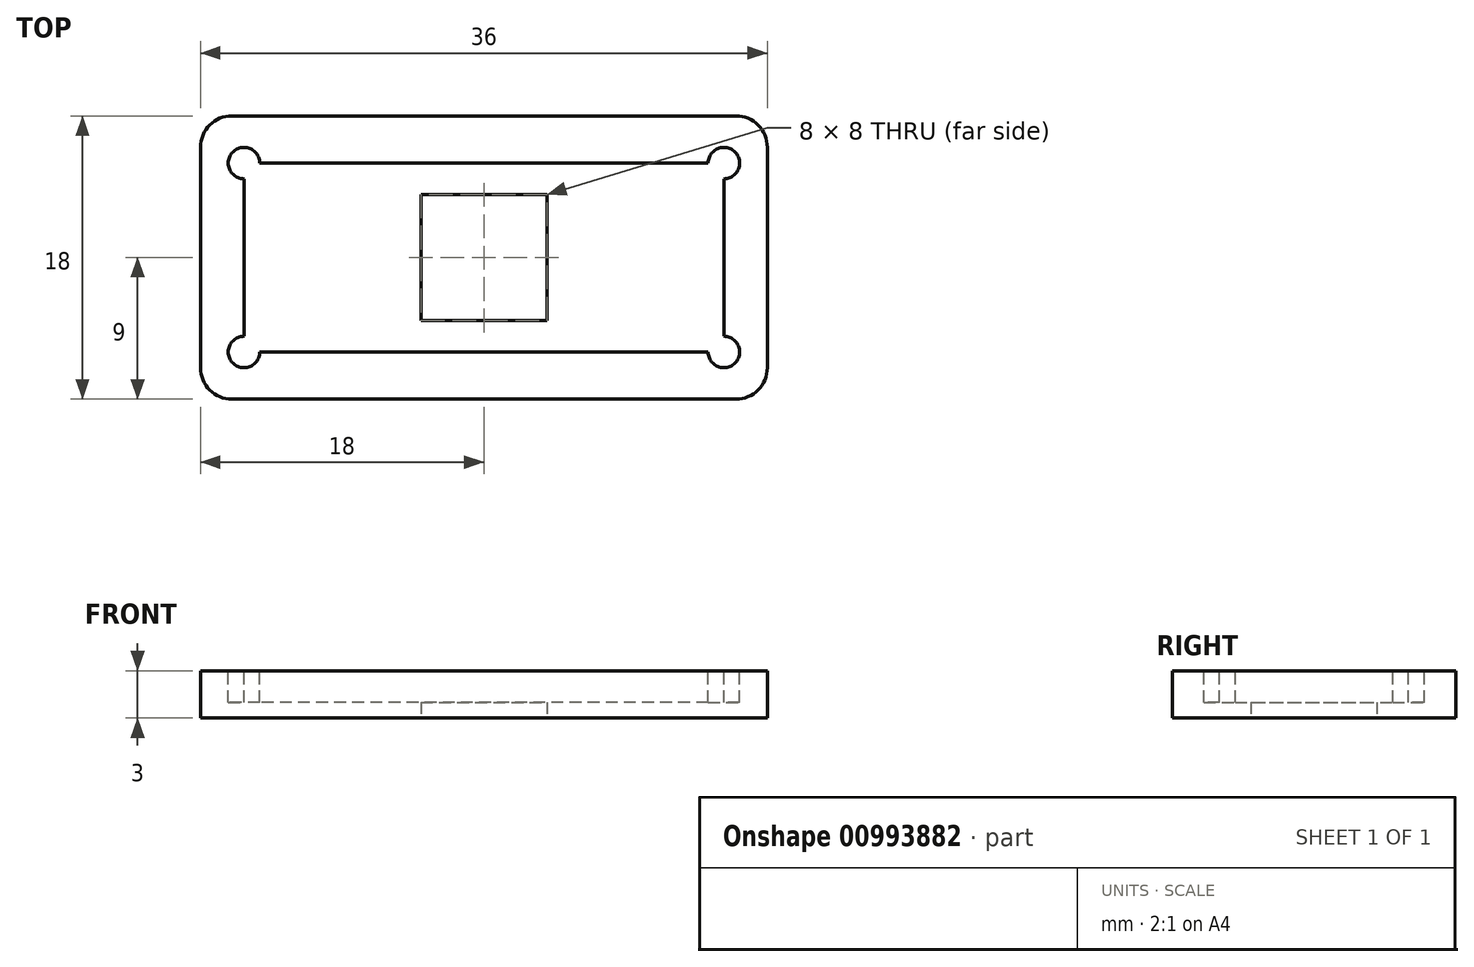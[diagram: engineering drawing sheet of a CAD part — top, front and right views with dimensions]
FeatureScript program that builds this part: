
annotation { "Feature Type Name" : "Feature", "Feature Type Description" : "" }
export const myFeature = defineFeature(function(context is Context, id is Id, definition is map)
    precondition{}
    {
        {
            var Q0;
            Q0=qCreatedBy(makeId("Top.planeOp"),FACE);
            var sketch = newSketch(context, id + "F0", { "sketchPlane" : qUnion([Q0])});
            skLineSegment(sketch, "E0.bottom", {"start": v(18, -9) * mm, "end": v(-18, -9) * mm});
            skLineSegment(sketch, "E0.top", {"start": v(18, 9) * mm, "end": v(-18, 9) * mm});
            skLineSegment(sketch, "E0.left", {"start": v(18, -9) * mm, "end": v(18, 9) * mm});
            skLineSegment(sketch, "E0.right", {"start": v(-18, -9) * mm, "end": v(-18, 9) * mm});
            skPoint(sketch, "E0.middle", {"position": v(0, 0) * mm});
            skSolve(sketch);
        }
        {
            var Q0;
            Q0=makeQuery(id+"F0.imprint","IMPRINT",FACE,{"disambiguationData":[TD([[makeQuery(id+"F0.imprint","IMPRINT",EDGE,{"derivedFrom":sQuery(id+"F0.wireOp",EDGE,"E0.bottom")}),-1.0]])]});
            extrude(context, id + "F1", {"entities" : qUnion([Q0]), "depth" : 3 * mm, "offsetDistance" : 25 * mm});
        }
        {
            var Q0;
            Q0=makeQuery(id+"F1.opExtrude","CAP_FACE",FACE,{"disambiguationData":[OSD([sQuery(id+"F0.wireOp",EDGE,"E0.bottom"),sQuery(id+"F0.wireOp",EDGE,"E0.top"),sQuery(id+"F0.wireOp",EDGE,"E0.left"),sQuery(id+"F0.wireOp",EDGE,"E0.right")])],"isStart":false});
            var sketch = newSketch(context, id + "F2", { "sketchPlane" : qUnion([Q0])});
            skLineSegment(sketch, "E1.bottom", {"start": v(15.24, -6) * mm, "end": v(-15.24, -6) * mm});
            skLineSegment(sketch, "E1.top", {"start": v(15.24, 6) * mm, "end": v(-15.24, 6) * mm});
            skLineSegment(sketch, "E1.left", {"start": v(15.24, -6) * mm, "end": v(15.24, 6) * mm});
            skLineSegment(sketch, "E1.right", {"start": v(-15.24, -6) * mm, "end": v(-15.24, 6) * mm});
            skPoint(sketch, "E1.middle", {"position": v(0, 0) * mm});
            skSolve(sketch);
        }
        {
            var Q0;
            Q0=makeQuery(id+"F2.imprint","IMPRINT",FACE,{"disambiguationData":[TD([[makeQuery(id+"F2.imprint","IMPRINT",EDGE,{"derivedFrom":sQuery(id+"F2.wireOp",EDGE,"E1.bottom")}),-1.0]])]});
            extrude(context, id + "F3", {"entities" : qUnion([Q0]), "operationType" : NewBodyOperationType.REMOVE, "oppositeDirection" : true, "depth" : 2 * mm, "offsetDistance" : 25 * mm});
        }
        {
            var Q0;
            Q0=makeQuery(id+"F1.opExtrude","CAP_FACE",FACE,{"disambiguationData":[OSD([sQuery(id+"F0.wireOp",EDGE,"E0.bottom"),sQuery(id+"F0.wireOp",EDGE,"E0.top"),sQuery(id+"F0.wireOp",EDGE,"E0.left"),sQuery(id+"F0.wireOp",EDGE,"E0.right")])],"isStart":true});
            var sketch = newSketch(context, id + "F4", { "sketchPlane" : qUnion([Q0])});
            skLineSegment(sketch, "E2.bottom", {"start": v(4, -4) * mm, "end": v(-4, -4) * mm});
            skLineSegment(sketch, "E2.top", {"start": v(4, 4) * mm, "end": v(-4, 4) * mm});
            skLineSegment(sketch, "E2.left", {"start": v(4, -4) * mm, "end": v(4, 4) * mm});
            skLineSegment(sketch, "E2.right", {"start": v(-4, -4) * mm, "end": v(-4, 4) * mm});
            skPoint(sketch, "E2.middle", {"position": v(0, 0) * mm});
            skSolve(sketch);
        }
        {
            var Q0;
            Q0 = qSketchRegion(id + "F4", true);
            extrude(context, id + "F5", {"entities" : qUnion([Q0]), "operationType" : NewBodyOperationType.REMOVE, "endBound" : BoundingType.THROUGH_ALL, "oppositeDirection" : true, "depth" : 25 * mm, "offsetDistance" : 25 * mm});
        }
        {
            var Q0;
            Q0=makeQuery(id+"F1.opExtrude","SWEPT_EDGE",EDGE,{"disambiguationData":[OSD([sQuery(id+"F0.wireOp",EDGE,"E0.bottom"),sQuery(id+"F0.wireOp",EDGE,"E0.right")])]});
            var Q1;
            Q1=makeQuery(id+"F1.opExtrude","SWEPT_EDGE",EDGE,{"disambiguationData":[OSD([sQuery(id+"F0.wireOp",EDGE,"E0.top"),sQuery(id+"F0.wireOp",EDGE,"E0.right")])]});
            var Q2;
            Q2=makeQuery(id+"F1.opExtrude","SWEPT_EDGE",EDGE,{"disambiguationData":[OSD([sQuery(id+"F0.wireOp",EDGE,"E0.bottom"),sQuery(id+"F0.wireOp",EDGE,"E0.left")])]});
            var Q3;
            Q3=makeQuery(id+"F1.opExtrude","SWEPT_EDGE",EDGE,{"disambiguationData":[OSD([sQuery(id+"F0.wireOp",EDGE,"E0.top"),sQuery(id+"F0.wireOp",EDGE,"E0.left")])]});
            fillet(context, id + "F6", {"entities" : qUnion([Q0, Q1, Q2, Q3]), "radius" : 2 * mm, "tangentPropagation" : true, "allowEdgeOverflow" : false});
        }
        {
            var Q0;
            Q0=makeQuery(id+"F1.opExtrude","CAP_FACE",FACE,{"disambiguationData":[OSD([sQuery(id+"F0.wireOp",EDGE,"E0.bottom"),sQuery(id+"F0.wireOp",EDGE,"E0.top"),sQuery(id+"F0.wireOp",EDGE,"E0.left"),sQuery(id+"F0.wireOp",EDGE,"E0.right")])],"isStart":false});
            var sketch = newSketch(context, id + "F7", { "sketchPlane" : qUnion([Q0])});
            skCircle(sketch, "E3", {"center": v(-15.24, 6) * mm, "radius": 1 * mm});
            skCircle(sketch, "E4", {"center": v(-15.24, -6) * mm, "radius": 1 * mm});
            skCircle(sketch, "E5", {"center": v(15.24, 6) * mm, "radius": 1 * mm});
            skCircle(sketch, "E6", {"center": v(15.24, -6) * mm, "radius": 1 * mm});
            skSolve(sketch);
        }
        {
            var Q0;
            Q0 = qSketchRegion(id + "F7", true);
            extrude(context, id + "F8", {"entities" : qUnion([Q0]), "operationType" : NewBodyOperationType.REMOVE, "oppositeDirection" : true, "depth" : 2 * mm, "offsetDistance" : 25 * mm});
        }
    });
